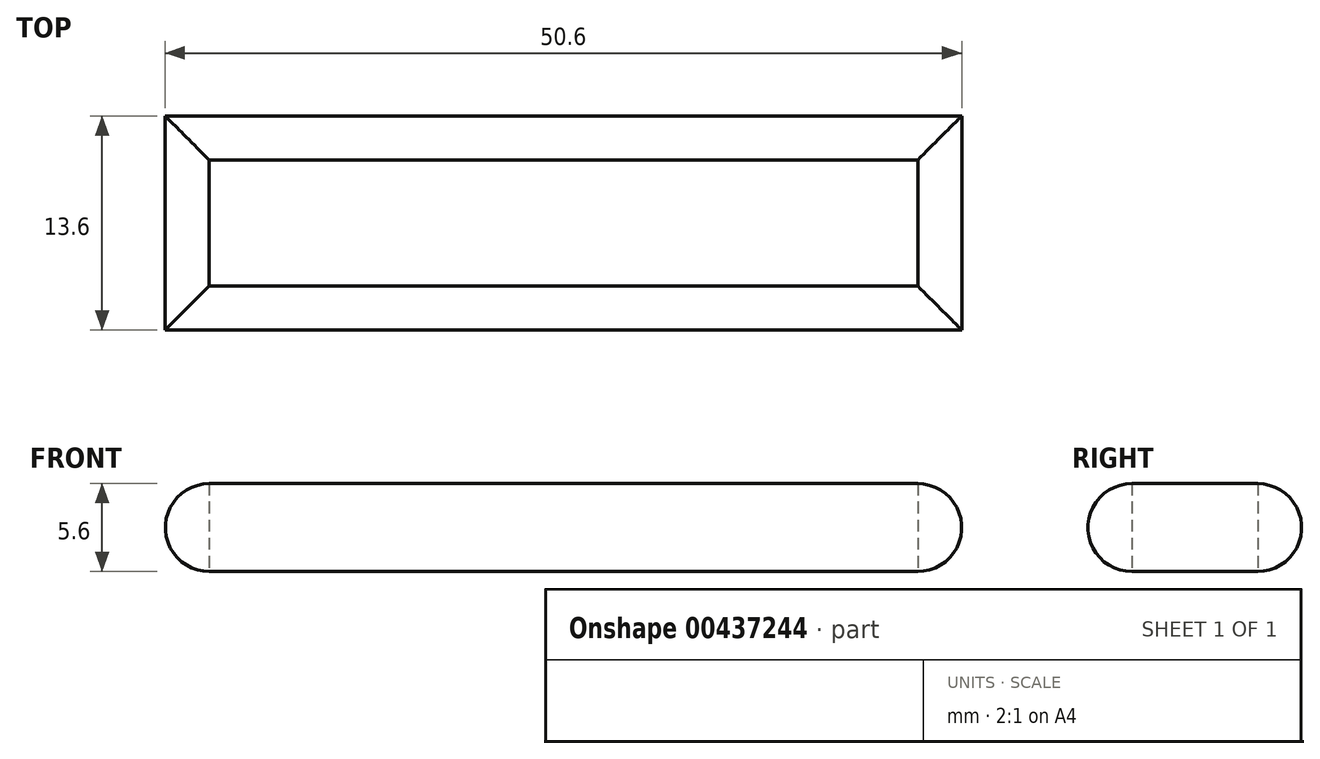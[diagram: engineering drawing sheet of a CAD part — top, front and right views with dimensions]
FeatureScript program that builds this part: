
annotation { "Feature Type Name" : "Feature", "Feature Type Description" : "" }
export const myFeature = defineFeature(function(context is Context, id is Id, definition is map)
    precondition{}
    {
        {
            var Q0;
            Q0=qCreatedBy(makeId("Top.planeOp"),FACE);
            var sketch = newSketch(context, id + "F0", { "sketchPlane" : qUnion([Q0])});
            skLineSegment(sketch, "E0.bottom", {"start": v(0, 0) * mm, "end": v(-45, 0) * mm});
            skLineSegment(sketch, "E0.top", {"start": v(0, 8) * mm, "end": v(-45, 8) * mm});
            skLineSegment(sketch, "E0.left", {"start": v(0, 0) * mm, "end": v(0, 8) * mm});
            skLineSegment(sketch, "E0.right", {"start": v(-45, 0) * mm, "end": v(-45, 8) * mm});
            skSolve(sketch);
        }
        {
            var Q0;
            Q0=qCreatedBy(makeId("Front.planeOp"),FACE);
            var sketch = newSketch(context, id + "F1", { "sketchPlane" : qUnion([Q0])});
            skLineSegment(sketch, "E1", {"start": v(0, 0) * mm, "end": v(0, 2.8) * mm});
            skLineSegment(sketch, "E2", {"start": v(0, 0) * mm, "end": v(0, -2.8) * mm});
            skArc(sketch, "E3", {"start": v(0, 2.8) * mm, "mid": v(2.8, 0) * mm, "end": v(0, -2.8) * mm});
            skSolve(sketch);
        }
        {
            var Q0;
            Q0=makeQuery(id+"F1.imprint","IMPRINT",FACE,{"disambiguationData":[TD([[makeQuery(id+"F1.imprint","IMPRINT",EDGE,{"derivedFrom":sQuery(id+"F1.wireOp",EDGE,"E1")}),-1.0]])]});
            var Q1;
            Q1=sQuery(id+"F0.wireOp",EDGE,"E0.left");
            var Q2;
            Q2=sQuery(id+"F0.wireOp",EDGE,"E0.bottom");
            var Q3;
            Q3=sQuery(id+"F0.wireOp",EDGE,"E0.top");
            var Q4;
            Q4=sQuery(id+"F0.wireOp",EDGE,"E0.right");
            sweep(context, id + "F2", {"profiles" : qUnion([Q0]), "path" : qUnion([Q1, Q2, Q3, Q4])});
        }
    });
